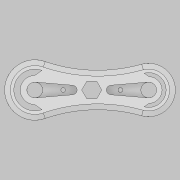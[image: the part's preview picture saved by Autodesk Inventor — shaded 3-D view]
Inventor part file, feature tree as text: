
AUTODESK INVENTOR PART (.ipt)
format: ipt  version: 2022.2 (Build 262287010, 287A)  size: 246,272 bytes
history: native  units: mm
features: extrude x6, sketch x5, other x1, chamfer x1
ambient origin geometry x8: Origin, YZ Plane, XZ Plane, XY Plane, X Axis, Y Axis, Z Axis, Center Point
bodies: Body1 (feature_tree)
feature tree (13):
  other  "Sólido1"
  extrude  "Extrusión1"  Depth=49.0mm
  extrude  "Extrusión2"  Depth=8.5mm
  extrude  "Extrusión3"  Depth=23.0mm
  extrude  "Extrusión4"  Depth=11.1mm
  extrude  "Extrusión5"  Depth=10.0mm
  extrude  "Extrusión6"  Depth=11.5mm
  chamfer  "Chaflán1"  Distance=4.0mm
  sketch  "Boceto1"  dims[d2=7.5mm d3=49.0mm]
  sketch  "Boceto2"  dims[d4=8.5mm d5=8.5mm]
  sketch  "Boceto4"  dims[d6=26.0mm d7=23.0mm]
  sketch  "Boceto5"  dims[d12=12.2mm d13=11.1mm]
  sketch  "Boceto6"  dims[d14=9.0mm d15=0.0mm d16=12.5mm d17=11.5mm d18=4.0mm d19=4.0mm d20=10.0mm d21=0.0mm d22=6.8mm d28=4.1mm d30=21.6mm d31=2.5mm d32=0.0mm d33=6.8mm d34=2.0mm d35=12.2mm d36=2.5mm d37=0.0mm d38=19.8mm d39=21.0mm d40=4.1mm d41=0.0mm d42=9.0mm d43=9.0mm d44=6.0mm d45=0.0mm d46=0.0mm d47=2.5mm d48=2.0mm d49=45.0deg]
